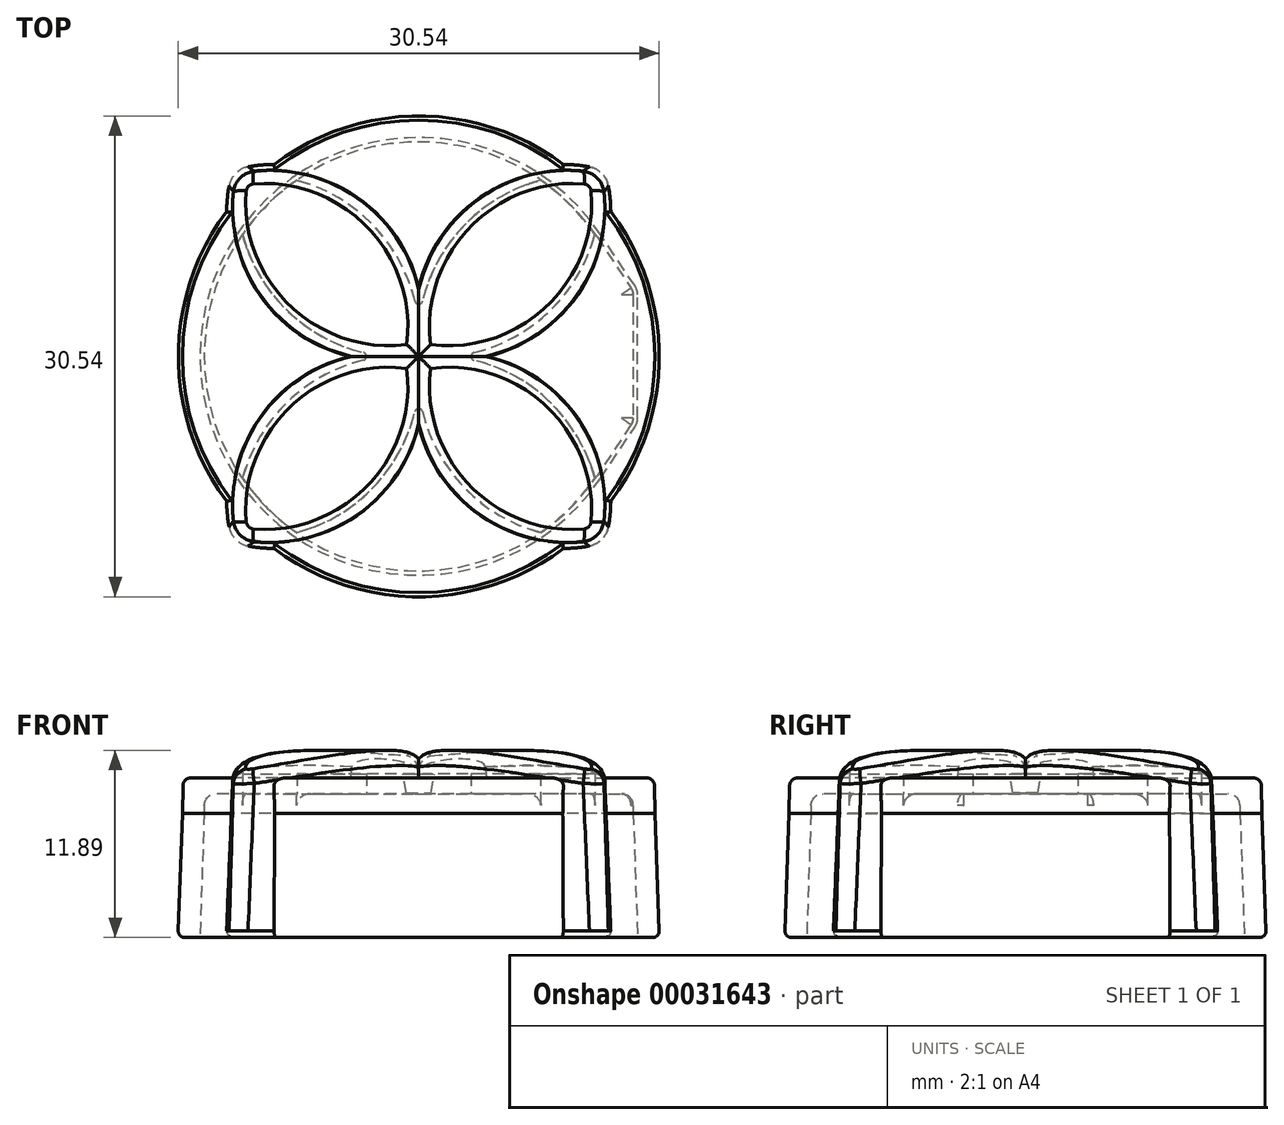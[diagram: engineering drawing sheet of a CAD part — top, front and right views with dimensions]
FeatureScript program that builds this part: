
annotation { "Feature Type Name" : "Feature", "Feature Type Description" : "" }
export const myFeature = defineFeature(function(context is Context, id is Id, definition is map)
    precondition{}
    {
        {
            var Q0;
            Q0=qCreatedBy(makeId("Top.planeOp"),FACE);
            cPlane(context, id + "F0", {"entities" : qUnion([Q0]), "cplaneType" : CPlaneType.OFFSET, "offset" : 8.73 * mm, "width" : 150 * mm, "height" : 150 * mm});
        }
        {
            var Q0;
            Q0=qCreatedBy(id+"F0.planeOp",FACE);
            var sketch = newSketch(context, id + "F1", { "sketchPlane" : qUnion([Q0])});
            skCircle(sketch, "E0", {"center": v(0, 0) * mm, "radius": 12.38 * mm});
            skCircle(sketch, "E1", {"center": v(0, 0) * mm, "radius": 13.38 * mm});
            skLineSegment(sketch, "E2.bottom", {"start": v(12.37, 4.08) * mm, "end": v(13.37, 4.08) * mm});
            skLineSegment(sketch, "E2.top", {"start": v(12.37, -4.07) * mm, "end": v(13.37, -4.07) * mm});
            skLineSegment(sketch, "E2.left", {"start": v(12.37, 3.91) * mm, "end": v(12.37, -3.91) * mm});
            skLineSegment(sketch, "E2.right", {"start": v(13.37, 3.92) * mm, "end": v(13.37, -3.92) * mm});
            skLineSegment(sketch, "E3", {"start": v(12.28, 4.2) * mm, "end": v(9.95, 7.35) * mm});
            skLineSegment(sketch, "E4", {"start": v(13.3, 4.2) * mm, "end": v(11.1, 7.46) * mm});
            skLineSegment(sketch, "E5", {"start": v(12.28, -4.2) * mm, "end": v(9.95, -7.35) * mm});
            skLineSegment(sketch, "E6", {"start": v(13.3, -4.2) * mm, "end": v(11.1, -7.46) * mm});
            skPoint(sketch, "E7.visualSharp", {"position": v(13.37, 4.08) * mm});
            skArc(sketch, "E7.filletArc", {"start": v(13.37, 3.92) * mm, "mid": v(13.35, 4.07) * mm, "end": v(13.3, 4.2) * mm});
            skPoint(sketch, "E8.visualSharp", {"position": v(13.37, -4.07) * mm});
            skArc(sketch, "E8.filletArc", {"start": v(13.3, -4.2) * mm, "mid": v(13.35, -4.07) * mm, "end": v(13.38, -3.92) * mm});
            skPoint(sketch, "E9.visualSharp", {"position": v(12.37, -4.07) * mm});
            skArc(sketch, "E9.filletArc", {"start": v(12.28, -4.2) * mm, "mid": v(12.35, -4.07) * mm, "end": v(12.38, -3.91) * mm});
            skPoint(sketch, "E10.visualSharp", {"position": v(12.37, 4.08) * mm});
            skArc(sketch, "E10.filletArc", {"start": v(12.38, 3.91) * mm, "mid": v(12.35, 4.07) * mm, "end": v(12.28, 4.2) * mm});
            skCircle(sketch, "E11.0", {"center": v(0, 0) * mm, "radius": 13.63 * mm});
            skLineSegment(sketch, "E12.0", {"start": v(13.5, 4.34) * mm, "end": v(11.31, 7.6) * mm});
            skArc(sketch, "E13.0", {"start": v(13.63, 3.92) * mm, "mid": v(13.6, 4.14) * mm, "end": v(13.5, 4.34) * mm});
            skLineSegment(sketch, "E14.0", {"start": v(13.63, 3.92) * mm, "end": v(13.63, -3.92) * mm});
            skArc(sketch, "E15.0", {"start": v(13.5, -4.34) * mm, "mid": v(13.6, -4.14) * mm, "end": v(13.63, -3.92) * mm});
            skLineSegment(sketch, "E16.0", {"start": v(13.5, -4.34) * mm, "end": v(11.31, -7.6) * mm});
            skCircle(sketch, "E17", {"center": v(0, 0) * mm, "radius": 15 * mm});
            skSolve(sketch);
        }
        {
            var Q0;
            {var subQ6=sQuery(id+"F1.wireOp",EDGE,"E12.0");Q0=makeQuery(id+"F1.imprint","IMPRINT",FACE,{"disambiguationData":[TD([[makeQuery(id+"F1.imprint","IMPRINT",EDGE,{"derivedFrom":subQ6}),-1.0]])]});}
            var Q1;
            {var subQ0=sQuery(id+"F1.wireOp",EDGE,"E0");var subQ3=makeQuery(id+"F1.imprint","INTERSECT",VERTEX,{"derivedFrom":[subQ0,sQuery(id+"F1.wireOp",EDGE,"E3")]});Q1=makeQuery(id+"F1.imprint","IMPRINT",FACE,{"disambiguationData":[TD([[makeQuery(id+"F1.imprint","IMPRINT",EDGE,{"disambiguationData":[TD([[subQ3,1.0]])],"derivedFrom":subQ0}),1.0]])]});}
            var Q2;
            {var subQ5=sQuery(id+"F1.wireOp",EDGE,"E4");var subQ7=sQuery(id+"F1.wireOp",EDGE,"E1");var subQ9=makeQuery(id+"F1.imprint","INTERSECT",VERTEX,{"derivedFrom":[subQ7,subQ5]});Q2=makeQuery(id+"F1.imprint","IMPRINT",FACE,{"disambiguationData":[TD([[makeQuery(id+"F1.imprint","IMPRINT",EDGE,{"disambiguationData":[TD([[subQ9,-1.0]])],"derivedFrom":subQ7}),-1.0]])]});}
            var Q3;
            {var subQ1=sQuery(id+"F1.wireOp",EDGE,"E3");Q3=makeQuery(id+"F1.imprint","IMPRINT",FACE,{"disambiguationData":[TD([[makeQuery(id+"F1.imprint","IMPRINT",EDGE,{"derivedFrom":subQ1}),-1.0]])]});}
            var Q4;
            {var subQ1=sQuery(id+"F1.wireOp",EDGE,"E3");Q4=makeQuery(id+"F1.imprint","IMPRINT",FACE,{"disambiguationData":[TD([[makeQuery(id+"F1.imprint","IMPRINT",EDGE,{"derivedFrom":subQ1}),1.0]])]});}
            var Q5;
            {var subQ3=sQuery(id+"F1.wireOp",EDGE,"E2.bottom");var subQ5=sQuery(id+"F1.wireOp",EDGE,"E7.filletArc");var subQ6=makeQuery(id+"F1.imprint","INTERSECT",VERTEX,{"derivedFrom":[subQ3,subQ5]});Q5=makeQuery(id+"F1.imprint","IMPRINT",FACE,{"disambiguationData":[TD([[makeQuery(id+"F1.imprint","IMPRINT",EDGE,{"disambiguationData":[TD([[subQ6,1.0]])],"derivedFrom":subQ3}),1.0]])]});}
            var Q6;
            {var subQ3=sQuery(id+"F1.wireOp",EDGE,"E2.bottom");var subQ5=sQuery(id+"F1.wireOp",EDGE,"E7.filletArc");var subQ6=makeQuery(id+"F1.imprint","INTERSECT",VERTEX,{"derivedFrom":[subQ3,subQ5]});Q6=makeQuery(id+"F1.imprint","IMPRINT",FACE,{"disambiguationData":[TD([[makeQuery(id+"F1.imprint","IMPRINT",EDGE,{"disambiguationData":[TD([[subQ6,1.0]])],"derivedFrom":subQ3}),-1.0]])]});}
            var Q7;
            {var subQ3=sQuery(id+"F1.wireOp",EDGE,"E2.bottom");var subQ5=sQuery(id+"F1.wireOp",EDGE,"E1");var subQ7=makeQuery(id+"F1.imprint","INTERSECT",VERTEX,{"derivedFrom":[subQ5,subQ3]});Q7=makeQuery(id+"F1.imprint","IMPRINT",FACE,{"disambiguationData":[TD([[makeQuery(id+"F1.imprint","IMPRINT",EDGE,{"disambiguationData":[TD([[subQ7,1.0]])],"derivedFrom":subQ5}),-1.0]])]});}
            var Q8;
            {var subQ1=sQuery(id+"F1.wireOp",EDGE,"E4");var subQ5=sQuery(id+"F1.wireOp",EDGE,"E1");var subQ6=makeQuery(id+"F1.imprint","INTERSECT",VERTEX,{"derivedFrom":[subQ5,subQ1]});Q8=makeQuery(id+"F1.imprint","IMPRINT",FACE,{"disambiguationData":[TD([[makeQuery(id+"F1.imprint","IMPRINT",EDGE,{"disambiguationData":[TD([[subQ6,1.0]])],"derivedFrom":subQ5}),-1.0]])]});}
            var Q9;
            {var subQ4=sQuery(id+"F1.wireOp",EDGE,"E12.0");Q9=makeQuery(id+"F1.imprint","IMPRINT",FACE,{"disambiguationData":[TD([[makeQuery(id+"F1.imprint","IMPRINT",EDGE,{"derivedFrom":subQ4}),1.0]])]});}
            var Q10;
            {var subQ2=sQuery(id+"F1.wireOp",EDGE,"E2.right");var subQ5=makeQuery(id+"F1.imprint","INTERSECT",VERTEX,{"derivedFrom":[sQuery(id+"F1.wireOp",EDGE,"E1"),subQ2]});Q10=makeQuery(id+"F1.imprint","IMPRINT",FACE,{"disambiguationData":[TD([[makeQuery(id+"F1.imprint","IMPRINT",EDGE,{"disambiguationData":[TD([[subQ5,1.0]])],"derivedFrom":subQ2}),1.0]])]});}
            var Q11;
            {var subQ1=sQuery(id+"F1.wireOp",EDGE,"E5");Q11=makeQuery(id+"F1.imprint","IMPRINT",FACE,{"disambiguationData":[TD([[makeQuery(id+"F1.imprint","IMPRINT",EDGE,{"derivedFrom":subQ1}),-1.0]])]});}
            var Q12;
            {var subQ3=sQuery(id+"F1.wireOp",EDGE,"E2.top");var subQ5=sQuery(id+"F1.wireOp",EDGE,"E8.filletArc");var subQ6=makeQuery(id+"F1.imprint","INTERSECT",VERTEX,{"derivedFrom":[subQ3,subQ5]});Q12=makeQuery(id+"F1.imprint","IMPRINT",FACE,{"disambiguationData":[TD([[makeQuery(id+"F1.imprint","IMPRINT",EDGE,{"disambiguationData":[TD([[subQ6,1.0]])],"derivedFrom":subQ3}),1.0]])]});}
            var Q13;
            {var subQ3=sQuery(id+"F1.wireOp",EDGE,"E2.top");var subQ5=sQuery(id+"F1.wireOp",EDGE,"E1");var subQ7=makeQuery(id+"F1.imprint","INTERSECT",VERTEX,{"derivedFrom":[subQ5,subQ3]});Q13=makeQuery(id+"F1.imprint","IMPRINT",FACE,{"disambiguationData":[TD([[makeQuery(id+"F1.imprint","IMPRINT",EDGE,{"disambiguationData":[TD([[subQ7,-1.0]])],"derivedFrom":subQ5}),-1.0]])]});}
            var Q14;
            {var subQ0=sQuery(id+"F1.wireOp",EDGE,"E15.0");Q14=makeQuery(id+"F1.imprint","IMPRINT",FACE,{"disambiguationData":[TD([[makeQuery(id+"F1.imprint","IMPRINT",EDGE,{"derivedFrom":subQ0}),1.0]])]});}
            var Q15;
            {var subQ1=sQuery(id+"F1.wireOp",EDGE,"E6");var subQ5=sQuery(id+"F1.wireOp",EDGE,"E1");var subQ6=makeQuery(id+"F1.imprint","INTERSECT",VERTEX,{"derivedFrom":[subQ5,subQ1]});Q15=makeQuery(id+"F1.imprint","IMPRINT",FACE,{"disambiguationData":[TD([[makeQuery(id+"F1.imprint","IMPRINT",EDGE,{"disambiguationData":[TD([[subQ6,-1.0]])],"derivedFrom":subQ5}),-1.0]])]});}
            var Q16;
            {var subQ3=sQuery(id+"F1.wireOp",EDGE,"E2.top");var subQ5=sQuery(id+"F1.wireOp",EDGE,"E8.filletArc");var subQ6=makeQuery(id+"F1.imprint","INTERSECT",VERTEX,{"derivedFrom":[subQ3,subQ5]});Q16=makeQuery(id+"F1.imprint","IMPRINT",FACE,{"disambiguationData":[TD([[makeQuery(id+"F1.imprint","IMPRINT",EDGE,{"disambiguationData":[TD([[subQ6,1.0]])],"derivedFrom":subQ3}),-1.0]])]});}
            extrude(context, id + "F2", {"entities" : qUnion([Q0, Q1, Q2, Q3, Q4, Q5, Q6, Q7, Q8, Q9, Q10, Q11, Q12, Q13, Q14, Q15, Q16]), "depth" : 2.25 * mm, "hasDraft" : true, "draftAngle" : 1 * degree, "draftPullDirection" : true});
        }
        {
            var Q0;
            {var subQ6=sQuery(id+"F1.wireOp",EDGE,"E12.0");Q0=makeQuery(id+"F1.imprint","IMPRINT",FACE,{"disambiguationData":[TD([[makeQuery(id+"F1.imprint","IMPRINT",EDGE,{"derivedFrom":subQ6}),-1.0]])]});}
            var Q1;
            {var subQ1=sQuery(id+"F1.wireOp",EDGE,"E3");Q1=makeQuery(id+"F1.imprint","IMPRINT",FACE,{"disambiguationData":[TD([[makeQuery(id+"F1.imprint","IMPRINT",EDGE,{"derivedFrom":subQ1}),-1.0]])]});}
            var Q2;
            {var subQ5=sQuery(id+"F1.wireOp",EDGE,"E4");var subQ7=sQuery(id+"F1.wireOp",EDGE,"E1");var subQ9=makeQuery(id+"F1.imprint","INTERSECT",VERTEX,{"derivedFrom":[subQ7,subQ5]});Q2=makeQuery(id+"F1.imprint","IMPRINT",FACE,{"disambiguationData":[TD([[makeQuery(id+"F1.imprint","IMPRINT",EDGE,{"disambiguationData":[TD([[subQ9,-1.0]])],"derivedFrom":subQ7}),-1.0]])]});}
            var Q3;
            {var subQ1=sQuery(id+"F1.wireOp",EDGE,"E3");Q3=makeQuery(id+"F1.imprint","IMPRINT",FACE,{"disambiguationData":[TD([[makeQuery(id+"F1.imprint","IMPRINT",EDGE,{"derivedFrom":subQ1}),1.0]])]});}
            var Q4;
            {var subQ0=sQuery(id+"F1.wireOp",EDGE,"E0");var subQ3=makeQuery(id+"F1.imprint","INTERSECT",VERTEX,{"derivedFrom":[subQ0,sQuery(id+"F1.wireOp",EDGE,"E3")]});Q4=makeQuery(id+"F1.imprint","IMPRINT",FACE,{"disambiguationData":[TD([[makeQuery(id+"F1.imprint","IMPRINT",EDGE,{"disambiguationData":[TD([[subQ3,1.0]])],"derivedFrom":subQ0}),1.0]])]});}
            var Q5;
            {var subQ1=sQuery(id+"F1.wireOp",EDGE,"E4");var subQ5=sQuery(id+"F1.wireOp",EDGE,"E1");var subQ6=makeQuery(id+"F1.imprint","INTERSECT",VERTEX,{"derivedFrom":[subQ5,subQ1]});Q5=makeQuery(id+"F1.imprint","IMPRINT",FACE,{"disambiguationData":[TD([[makeQuery(id+"F1.imprint","IMPRINT",EDGE,{"disambiguationData":[TD([[subQ6,1.0]])],"derivedFrom":subQ5}),-1.0]])]});}
            var Q6;
            {var subQ4=sQuery(id+"F1.wireOp",EDGE,"E12.0");Q6=makeQuery(id+"F1.imprint","IMPRINT",FACE,{"disambiguationData":[TD([[makeQuery(id+"F1.imprint","IMPRINT",EDGE,{"derivedFrom":subQ4}),1.0]])]});}
            var Q7;
            {var subQ3=sQuery(id+"F1.wireOp",EDGE,"E2.bottom");var subQ5=sQuery(id+"F1.wireOp",EDGE,"E7.filletArc");var subQ6=makeQuery(id+"F1.imprint","INTERSECT",VERTEX,{"derivedFrom":[subQ3,subQ5]});Q7=makeQuery(id+"F1.imprint","IMPRINT",FACE,{"disambiguationData":[TD([[makeQuery(id+"F1.imprint","IMPRINT",EDGE,{"disambiguationData":[TD([[subQ6,1.0]])],"derivedFrom":subQ3}),1.0]])]});}
            var Q8;
            {var subQ3=sQuery(id+"F1.wireOp",EDGE,"E2.bottom");var subQ5=sQuery(id+"F1.wireOp",EDGE,"E7.filletArc");var subQ6=makeQuery(id+"F1.imprint","INTERSECT",VERTEX,{"derivedFrom":[subQ3,subQ5]});Q8=makeQuery(id+"F1.imprint","IMPRINT",FACE,{"disambiguationData":[TD([[makeQuery(id+"F1.imprint","IMPRINT",EDGE,{"disambiguationData":[TD([[subQ6,1.0]])],"derivedFrom":subQ3}),-1.0]])]});}
            var Q9;
            {var subQ3=sQuery(id+"F1.wireOp",EDGE,"E2.bottom");var subQ5=sQuery(id+"F1.wireOp",EDGE,"E1");var subQ7=makeQuery(id+"F1.imprint","INTERSECT",VERTEX,{"derivedFrom":[subQ5,subQ3]});Q9=makeQuery(id+"F1.imprint","IMPRINT",FACE,{"disambiguationData":[TD([[makeQuery(id+"F1.imprint","IMPRINT",EDGE,{"disambiguationData":[TD([[subQ7,1.0]])],"derivedFrom":subQ5}),-1.0]])]});}
            var Q10;
            {var subQ2=sQuery(id+"F1.wireOp",EDGE,"E2.right");var subQ5=makeQuery(id+"F1.imprint","INTERSECT",VERTEX,{"derivedFrom":[sQuery(id+"F1.wireOp",EDGE,"E1"),subQ2]});Q10=makeQuery(id+"F1.imprint","IMPRINT",FACE,{"disambiguationData":[TD([[makeQuery(id+"F1.imprint","IMPRINT",EDGE,{"disambiguationData":[TD([[subQ5,1.0]])],"derivedFrom":subQ2}),1.0]])]});}
            var Q11;
            {var subQ1=sQuery(id+"F1.wireOp",EDGE,"E5");Q11=makeQuery(id+"F1.imprint","IMPRINT",FACE,{"disambiguationData":[TD([[makeQuery(id+"F1.imprint","IMPRINT",EDGE,{"derivedFrom":subQ1}),-1.0]])]});}
            var Q12;
            {var subQ3=sQuery(id+"F1.wireOp",EDGE,"E2.top");var subQ5=sQuery(id+"F1.wireOp",EDGE,"E8.filletArc");var subQ6=makeQuery(id+"F1.imprint","INTERSECT",VERTEX,{"derivedFrom":[subQ3,subQ5]});Q12=makeQuery(id+"F1.imprint","IMPRINT",FACE,{"disambiguationData":[TD([[makeQuery(id+"F1.imprint","IMPRINT",EDGE,{"disambiguationData":[TD([[subQ6,1.0]])],"derivedFrom":subQ3}),1.0]])]});}
            var Q13;
            {var subQ3=sQuery(id+"F1.wireOp",EDGE,"E2.top");var subQ5=sQuery(id+"F1.wireOp",EDGE,"E1");var subQ7=makeQuery(id+"F1.imprint","INTERSECT",VERTEX,{"derivedFrom":[subQ5,subQ3]});Q13=makeQuery(id+"F1.imprint","IMPRINT",FACE,{"disambiguationData":[TD([[makeQuery(id+"F1.imprint","IMPRINT",EDGE,{"disambiguationData":[TD([[subQ7,-1.0]])],"derivedFrom":subQ5}),-1.0]])]});}
            var Q14;
            {var subQ0=sQuery(id+"F1.wireOp",EDGE,"E15.0");Q14=makeQuery(id+"F1.imprint","IMPRINT",FACE,{"disambiguationData":[TD([[makeQuery(id+"F1.imprint","IMPRINT",EDGE,{"derivedFrom":subQ0}),1.0]])]});}
            var Q15;
            {var subQ3=sQuery(id+"F1.wireOp",EDGE,"E2.top");var subQ5=sQuery(id+"F1.wireOp",EDGE,"E8.filletArc");var subQ6=makeQuery(id+"F1.imprint","INTERSECT",VERTEX,{"derivedFrom":[subQ3,subQ5]});Q15=makeQuery(id+"F1.imprint","IMPRINT",FACE,{"disambiguationData":[TD([[makeQuery(id+"F1.imprint","IMPRINT",EDGE,{"disambiguationData":[TD([[subQ6,1.0]])],"derivedFrom":subQ3}),-1.0]])]});}
            var Q16;
            {var subQ1=sQuery(id+"F1.wireOp",EDGE,"E6");var subQ5=sQuery(id+"F1.wireOp",EDGE,"E1");var subQ6=makeQuery(id+"F1.imprint","INTERSECT",VERTEX,{"derivedFrom":[subQ5,subQ1]});Q16=makeQuery(id+"F1.imprint","IMPRINT",FACE,{"disambiguationData":[TD([[makeQuery(id+"F1.imprint","IMPRINT",EDGE,{"disambiguationData":[TD([[subQ6,-1.0]])],"derivedFrom":subQ5}),-1.0]])]});}
            extrude(context, id + "F3", {"entities" : qUnion([Q0, Q1, Q2, Q3, Q4, Q5, Q6, Q7, Q8, Q9, Q10, Q11, Q12, Q13, Q14, Q15, Q16]), "operationType" : NewBodyOperationType.ADD, "oppositeDirection" : true, "depth" : 7.88 * mm, "hasDraft" : true, "draftAngle" : 2 * degree});
        }
        {
            var Q0;
            Q0=qCreatedBy(makeId("Top.planeOp"),FACE);
            var sketch = newSketch(context, id + "F4", { "sketchPlane" : qUnion([Q0])});
            skLineSegment(sketch, "E18", {"start": v(0, 0) * mm, "end": v(0, 19.92) * mm, "construction": true});
            skLineSegment(sketch, "E19", {"start": v(0, 0) * mm, "end": v(17.2, 17.2) * mm, "construction": true});
            skArc(sketch, "E20", {"start": v(11.84, 11.84) * mm, "mid": v(2.38, 9.47) * mm, "end": v(0, 0) * mm});
            skArc(sketch, "E21.0.MirrorCS", {"start": v(11.84, 11.84) * mm, "mid": v(9.47, 2.38) * mm, "end": v(0, 0) * mm});
            skPoint(sketch, "E22.center", {"position": v(0, 0) * mm});
            skLineSegment(sketch, "E22.anchor1", {"start": v(0, 0) * mm, "end": v(0, 0) * mm});
            skLineSegment(sketch, "E22.anchor2", {"start": v(0, 0) * mm, "end": v(21.18, 0) * mm, "construction": true});
            skSolve(sketch);
        }
        {
            var Q0;
            Q0=qCreatedBy(makeId("Top.planeOp"),FACE);
            cPlane(context, id + "F5", {"entities" : qUnion([Q0]), "cplaneType" : CPlaneType.OFFSET, "offset" : 13.98 * mm, "width" : 150 * mm, "height" : 150 * mm});
        }
        {
            var Q0;
            Q0=qCreatedBy(id+"F5.planeOp",FACE);
            var sketch = newSketch(context, id + "F6", { "sketchPlane" : qUnion([Q0])});
            skLineSegment(sketch, "E23", {"start": v(0, 0) * mm, "end": v(0, 1.45) * mm, "construction": true});
            skLineSegment(sketch, "E24", {"start": v(0, 0) * mm, "end": v(22.98, 22.98) * mm, "construction": true});
            skArc(sketch, "E25", {"start": v(11.5, 11.5) * mm, "mid": v(2.63, 8.86) * mm, "end": v(0, 0) * mm});
            skArc(sketch, "E26", {"start": v(11.84, 11.84) * mm, "mid": v(2.71, 9.13) * mm, "end": v(0, 0) * mm, "construction": true});
            skArc(sketch, "E27.0.MirrorCS", {"start": v(11.5, 11.5) * mm, "mid": v(8.86, 2.63) * mm, "end": v(0, 0) * mm});
            skSolve(sketch);
        }
        {
            var Q1;
            Q1=makeQuery(id+"F4.imprint","IMPRINT",FACE,{"disambiguationData":[TD([[makeQuery(id+"F4.imprint","IMPRINT",EDGE,{"derivedFrom":sQuery(id+"F4.wireOp",EDGE,"E20")}),1.0]])]});
            var Q2;
            Q2=makeQuery(id+"F6.imprint","IMPRINT",FACE,{"disambiguationData":[TD([[makeQuery(id+"F6.imprint","IMPRINT",EDGE,{"derivedFrom":sQuery(id+"F6.wireOp",EDGE,"E25")}),1.0]])]});
            loft(context, id + "F7", {"sheetProfilesArray" : [{ "sheetProfileEntities" : qUnion([Q1]) }, { "sheetProfileEntities" : qUnion([Q2]) }]});
        }
        {
            var Q0;
            Q0=qCreatedBy(makeId("Front.planeOp"),FACE);
            var Q1;
            Q1=qCreatedBy(makeId("Right.planeOp"),FACE);
            cPlane(context, id + "F8", {"entities" : qUnion([Q0, Q1]), "cplaneType" : CPlaneType.MID_PLANE, "offset" : 150 * mm, "flipAlignment" : true, "width" : 150 * mm, "height" : 150 * mm});
        }
        {
            var Q0;
            Q0=qCreatedBy(id+"F8.planeOp",FACE);
            var sketch = newSketch(context, id + "F9", { "sketchPlane" : qUnion([Q0])});
            skLineSegment(sketch, "E28", {"start": v(0, 0) * mm, "end": v(0, 14) * mm});
            skLineSegment(sketch, "E29", {"start": v(0, 0.85) * mm, "end": v(16.75, 0.85) * mm});
            skLineSegment(sketch, "E30", {"start": v(0, 11.23) * mm, "end": v(23.83, 11.23) * mm, "construction": true});
            skLineSegment(sketch, "E31", {"start": v(16.75, 0.85) * mm, "end": v(16.37, 11.24) * mm});
            skLineSegment(sketch, "E32", {"start": v(16.75, 0.85) * mm, "end": v(16.75, 14) * mm});
            skLineSegment(sketch, "E33", {"start": v(0, 14) * mm, "end": v(16.75, 14) * mm});
            skLineSegment(sketch, "E34", {"start": v(16.75, 0.85) * mm, "end": v(16.75, -1.44) * mm});
            skLineSegment(sketch, "E35", {"start": v(16.75, -1.44) * mm, "end": v(0, -1.44) * mm});
            skLineSegment(sketch, "E36", {"start": v(0, -1.44) * mm, "end": v(0, 0.85) * mm});
            skArc(sketch, "E37", {"start": v(16.38, 11.24) * mm, "mid": v(8.24, 12.67) * mm, "end": v(0, 12.23) * mm});
            skLineSegment(sketch, "E38", {"start": v(0, 12.73) * mm, "end": v(27.33, 12.73) * mm, "construction": true});
            skSolve(sketch);
        }
        {
            var Q0;
            Q0=makeQuery(id+"F9.imprint","IMPRINT",FACE,{"disambiguationData":[TD([[makeQuery(id+"F9.imprint","IMPRINT",EDGE,{"derivedFrom":sQuery(id+"F9.wireOp",EDGE,"E31")}),-1.0]])]});
            var Q1;
            {var subQ2=sQuery(id+"F9.wireOp",EDGE,"E29");Q1=makeQuery(id+"F9.imprint","IMPRINT",FACE,{"disambiguationData":[TD([[makeQuery(id+"F9.imprint","IMPRINT",EDGE,{"derivedFrom":subQ2}),-1.0]])]});}
            extrude(context, id + "F10", {"entities" : qUnion([Q0, Q1]), "operationType" : NewBodyOperationType.REMOVE, "endBound" : BoundingType.SYMMETRIC, "oppositeDirection" : true, "depth" : 12 * mm});
        }
        {
            var Q0;
            {var subQ0=sQuery(id+"F4.wireOp",EDGE,"E20");var subQ1=sQuery(id+"F4.wireOp",EDGE,"E21.0.MirrorCS");var subQ2=sQuery(id+"F6.wireOp",EDGE,"E25");var subQ3=sQuery(id+"F6.wireOp",EDGE,"E27.0.MirrorCS");Q0=makeQuery(id+"F7.opLoft","SWEPT_EDGE",EDGE,{"disambiguationData":[OSD([subQ0,subQ1,subQ2,subQ3]),TDD([makeQuery(id+"F4.imprint","INTERSECT",VERTEX,{"disambiguationData":[OD(0.0)],"derivedFrom":[subQ0,subQ1]}),makeQuery(id+"F6.imprint","INTERSECT",VERTEX,{"disambiguationData":[OD(0.0)],"derivedFrom":[subQ2,subQ3]})])]});}
            fillet(context, id + "F11", {"entities" : qUnion([Q0]), "radius" : 1.5 * mm, "tangentPropagation" : true, "allowEdgeOverflow" : false});
        }
        {
            var Q0;
            {var subQ0=sQuery(id+"F4.wireOp",EDGE,"E20");var subQ1=sQuery(id+"F4.wireOp",EDGE,"E21.0.MirrorCS");var subQ2=sQuery(id+"F6.wireOp",EDGE,"E25");var subQ3=sQuery(id+"F6.wireOp",EDGE,"E27.0.MirrorCS");Q0=makeQuery(id+"F10.boolean.opBoolean","INTERSECT",EDGE,{"derivedFrom":[makeQuery(id+"F7.opLoft","SWEPT_FACE",FACE,{"disambiguationData":[OSD([subQ0,subQ1,subQ2,subQ3]),TDD([makeQuery(id+"F4.imprint","INTERSECT",VERTEX,{"disambiguationData":[OD(0.0)],"derivedFrom":[subQ0,subQ1]}),makeQuery(id+"F4.imprint","INTERSECT",VERTEX,{"disambiguationData":[OD(1.0)],"derivedFrom":[subQ0,subQ1]}),makeQuery(id+"F4.imprint","IMPRINT",EDGE,{"derivedFrom":subQ1}),makeQuery(id+"F6.imprint","INTERSECT",VERTEX,{"disambiguationData":[OD(0.0)],"derivedFrom":[subQ2,subQ3]}),makeQuery(id+"F6.imprint","INTERSECT",VERTEX,{"disambiguationData":[OD(1.0)],"derivedFrom":[subQ2,subQ3]}),makeQuery(id+"F6.imprint","IMPRINT",EDGE,{"derivedFrom":subQ3})])]}),makeQuery(id+"F10.opExtrude","SWEPT_FACE",FACE,{"disambiguationData":[OSD([sQuery(id+"F9.wireOp",EDGE,"E37")])]})]});}
            fillet(context, id + "F12", {"entities" : qUnion([Q0]), "radius" : 1 * mm, "tangentPropagation" : true, "allowEdgeOverflow" : false});
        }
        {
            var Q0;
            Q0=makeQuery(id+"F7.opLoft","SWEPT_BODY",BODY,{"disambiguationData":[OSD([makeQuery(id+"F4.imprint","IMPRINT",FACE,{"disambiguationData":[TD([[makeQuery(id+"F4.imprint","IMPRINT",EDGE,{"derivedFrom":sQuery(id+"F4.wireOp",EDGE,"E20")}),1.0]])]}),makeQuery(id+"F6.imprint","IMPRINT",FACE,{"disambiguationData":[TD([[makeQuery(id+"F6.imprint","IMPRINT",EDGE,{"derivedFrom":sQuery(id+"F6.wireOp",EDGE,"E25")}),1.0]])]})])]});
            var Q1;
            Q1=sQuery(id+"F9.wireOp",EDGE,"E28");
            circularPattern(context, id + "F13", {"operationType" : NewBodyOperationType.ADD, "entities" : qUnion([Q0]), "axis" : qUnion([Q1]), "angle" : 90 * degree, "instanceCount" : round(4)});
        }
        {
            var Q0;
            {var subQ0=sQuery(id+"F1.wireOp",EDGE,"E0");var subQ3=makeQuery(id+"F1.imprint","INTERSECT",VERTEX,{"derivedFrom":[subQ0,sQuery(id+"F1.wireOp",EDGE,"E3")]});Q0=makeQuery(id+"F1.imprint","IMPRINT",FACE,{"disambiguationData":[TD([[makeQuery(id+"F1.imprint","IMPRINT",EDGE,{"disambiguationData":[TD([[subQ3,1.0]])],"derivedFrom":subQ0}),1.0]])]});}
            var Q1;
            {var subQ1=sQuery(id+"F1.wireOp",EDGE,"E3");Q1=makeQuery(id+"F1.imprint","IMPRINT",FACE,{"disambiguationData":[TD([[makeQuery(id+"F1.imprint","IMPRINT",EDGE,{"derivedFrom":subQ1}),-1.0]])]});}
            var Q2;
            {var subQ5=sQuery(id+"F1.wireOp",EDGE,"E4");var subQ7=sQuery(id+"F1.wireOp",EDGE,"E1");var subQ9=makeQuery(id+"F1.imprint","INTERSECT",VERTEX,{"derivedFrom":[subQ7,subQ5]});Q2=makeQuery(id+"F1.imprint","IMPRINT",FACE,{"disambiguationData":[TD([[makeQuery(id+"F1.imprint","IMPRINT",EDGE,{"disambiguationData":[TD([[subQ9,-1.0]])],"derivedFrom":subQ7}),-1.0]])]});}
            var Q3;
            {var subQ4=sQuery(id+"F1.wireOp",EDGE,"E12.0");Q3=makeQuery(id+"F1.imprint","IMPRINT",FACE,{"disambiguationData":[TD([[makeQuery(id+"F1.imprint","IMPRINT",EDGE,{"derivedFrom":subQ4}),1.0]])]});}
            var Q4;
            {var subQ3=sQuery(id+"F1.wireOp",EDGE,"E2.bottom");var subQ5=sQuery(id+"F1.wireOp",EDGE,"E7.filletArc");var subQ6=makeQuery(id+"F1.imprint","INTERSECT",VERTEX,{"derivedFrom":[subQ3,subQ5]});Q4=makeQuery(id+"F1.imprint","IMPRINT",FACE,{"disambiguationData":[TD([[makeQuery(id+"F1.imprint","IMPRINT",EDGE,{"disambiguationData":[TD([[subQ6,1.0]])],"derivedFrom":subQ3}),1.0]])]});}
            var Q5;
            {var subQ3=sQuery(id+"F1.wireOp",EDGE,"E2.bottom");var subQ5=sQuery(id+"F1.wireOp",EDGE,"E7.filletArc");var subQ6=makeQuery(id+"F1.imprint","INTERSECT",VERTEX,{"derivedFrom":[subQ3,subQ5]});Q5=makeQuery(id+"F1.imprint","IMPRINT",FACE,{"disambiguationData":[TD([[makeQuery(id+"F1.imprint","IMPRINT",EDGE,{"disambiguationData":[TD([[subQ6,1.0]])],"derivedFrom":subQ3}),-1.0]])]});}
            var Q6;
            {var subQ1=sQuery(id+"F1.wireOp",EDGE,"E3");Q6=makeQuery(id+"F1.imprint","IMPRINT",FACE,{"disambiguationData":[TD([[makeQuery(id+"F1.imprint","IMPRINT",EDGE,{"derivedFrom":subQ1}),1.0]])]});}
            var Q7;
            {var subQ3=sQuery(id+"F1.wireOp",EDGE,"E2.bottom");var subQ5=sQuery(id+"F1.wireOp",EDGE,"E1");var subQ7=makeQuery(id+"F1.imprint","INTERSECT",VERTEX,{"derivedFrom":[subQ5,subQ3]});Q7=makeQuery(id+"F1.imprint","IMPRINT",FACE,{"disambiguationData":[TD([[makeQuery(id+"F1.imprint","IMPRINT",EDGE,{"disambiguationData":[TD([[subQ7,1.0]])],"derivedFrom":subQ5}),-1.0]])]});}
            var Q8;
            {var subQ1=sQuery(id+"F1.wireOp",EDGE,"E4");var subQ5=sQuery(id+"F1.wireOp",EDGE,"E1");var subQ6=makeQuery(id+"F1.imprint","INTERSECT",VERTEX,{"derivedFrom":[subQ5,subQ1]});Q8=makeQuery(id+"F1.imprint","IMPRINT",FACE,{"disambiguationData":[TD([[makeQuery(id+"F1.imprint","IMPRINT",EDGE,{"disambiguationData":[TD([[subQ6,1.0]])],"derivedFrom":subQ5}),-1.0]])]});}
            var Q9;
            {var subQ1=sQuery(id+"F1.wireOp",EDGE,"E5");Q9=makeQuery(id+"F1.imprint","IMPRINT",FACE,{"disambiguationData":[TD([[makeQuery(id+"F1.imprint","IMPRINT",EDGE,{"derivedFrom":subQ1}),-1.0]])]});}
            var Q10;
            {var subQ3=sQuery(id+"F1.wireOp",EDGE,"E2.top");var subQ5=sQuery(id+"F1.wireOp",EDGE,"E1");var subQ7=makeQuery(id+"F1.imprint","INTERSECT",VERTEX,{"derivedFrom":[subQ5,subQ3]});Q10=makeQuery(id+"F1.imprint","IMPRINT",FACE,{"disambiguationData":[TD([[makeQuery(id+"F1.imprint","IMPRINT",EDGE,{"disambiguationData":[TD([[subQ7,-1.0]])],"derivedFrom":subQ5}),-1.0]])]});}
            var Q11;
            {var subQ1=sQuery(id+"F1.wireOp",EDGE,"E6");var subQ5=sQuery(id+"F1.wireOp",EDGE,"E1");var subQ6=makeQuery(id+"F1.imprint","INTERSECT",VERTEX,{"derivedFrom":[subQ5,subQ1]});Q11=makeQuery(id+"F1.imprint","IMPRINT",FACE,{"disambiguationData":[TD([[makeQuery(id+"F1.imprint","IMPRINT",EDGE,{"disambiguationData":[TD([[subQ6,-1.0]])],"derivedFrom":subQ5}),-1.0]])]});}
            var Q12;
            {var subQ3=sQuery(id+"F1.wireOp",EDGE,"E2.top");var subQ5=sQuery(id+"F1.wireOp",EDGE,"E8.filletArc");var subQ6=makeQuery(id+"F1.imprint","INTERSECT",VERTEX,{"derivedFrom":[subQ3,subQ5]});Q12=makeQuery(id+"F1.imprint","IMPRINT",FACE,{"disambiguationData":[TD([[makeQuery(id+"F1.imprint","IMPRINT",EDGE,{"disambiguationData":[TD([[subQ6,1.0]])],"derivedFrom":subQ3}),-1.0]])]});}
            var Q13;
            {var subQ0=sQuery(id+"F1.wireOp",EDGE,"E15.0");Q13=makeQuery(id+"F1.imprint","IMPRINT",FACE,{"disambiguationData":[TD([[makeQuery(id+"F1.imprint","IMPRINT",EDGE,{"derivedFrom":subQ0}),1.0]])]});}
            var Q14;
            {var subQ3=sQuery(id+"F1.wireOp",EDGE,"E2.top");var subQ5=sQuery(id+"F1.wireOp",EDGE,"E8.filletArc");var subQ6=makeQuery(id+"F1.imprint","INTERSECT",VERTEX,{"derivedFrom":[subQ3,subQ5]});Q14=makeQuery(id+"F1.imprint","IMPRINT",FACE,{"disambiguationData":[TD([[makeQuery(id+"F1.imprint","IMPRINT",EDGE,{"disambiguationData":[TD([[subQ6,1.0]])],"derivedFrom":subQ3}),1.0]])]});}
            var Q15;
            {var subQ2=sQuery(id+"F1.wireOp",EDGE,"E2.right");var subQ5=makeQuery(id+"F1.imprint","INTERSECT",VERTEX,{"derivedFrom":[sQuery(id+"F1.wireOp",EDGE,"E1"),subQ2]});Q15=makeQuery(id+"F1.imprint","IMPRINT",FACE,{"disambiguationData":[TD([[makeQuery(id+"F1.imprint","IMPRINT",EDGE,{"disambiguationData":[TD([[subQ5,1.0]])],"derivedFrom":subQ2}),1.0]])]});}
            extrude(context, id + "F14", {"entities" : qUnion([Q0, Q1, Q2, Q3, Q4, Q5, Q6, Q7, Q8, Q9, Q10, Q11, Q12, Q13, Q14, Q15]), "operationType" : NewBodyOperationType.REMOVE, "depth" : 1.25 * mm, "hasDraft" : true, "draftAngle" : 1 * degree, "draftPullDirection" : true, "hasSecondDirection" : true, "secondDirectionBound" : SecondDirectionBoundingType.THROUGH_ALL, "secondDirectionOppositeDirection" : true, "secondDirectionDepth" : 25 * mm, "hasSecondDirectionDraft" : true, "secondDirectionDraftAngle" : 2 * degree});
        }
        {
            var Q0;
            Q0=makeQuery(id+"F14.boolean.opBoolean","COPY",FACE,{"disambiguationData":[OD(0.0)],"derivedFrom":makeQuery(id+"F14.opExtrude","CAP_FACE",FACE,{"disambiguationData":[OSD([sQuery(id+"F1.wireOp",EDGE,"E11.0"),sQuery(id+"F1.wireOp",EDGE,"E12.0"),sQuery(id+"F1.wireOp",EDGE,"E13.0"),sQuery(id+"F1.wireOp",EDGE,"E14.0"),sQuery(id+"F1.wireOp",EDGE,"E15.0"),sQuery(id+"F1.wireOp",EDGE,"E16.0")])],"isStart":false})});
            var sketch = newSketch(context, id + "F15", { "sketchPlane" : qUnion([Q0])});
            skLineSegment(sketch, "E39", {"start": v(0, 0) * mm, "end": v(14.5, 14.5) * mm, "construction": true});
            skPoint(sketch, "E40.center", {"position": v(0, 0) * mm});
            skLineSegment(sketch, "E41", {"start": v(-34.97, -4.74) * mm, "end": v(-34.97, -3.29) * mm, "construction": true});
            skLineSegment(sketch, "E42", {"start": v(-34.97, -4.74) * mm, "end": v(-11.99, 18.24) * mm, "construction": true});
            skArc(sketch, "E43", {"start": v(-23.48, 6.75) * mm, "mid": v(-32.33, 4.11) * mm, "end": v(-34.97, -4.74) * mm});
            skArc(sketch, "E44", {"start": v(-23.12, 7.1) * mm, "mid": v(-32.25, 4.39) * mm, "end": v(-34.97, -4.74) * mm, "construction": true});
            skArc(sketch, "E45.0.MirrorCS", {"start": v(-23.48, 6.75) * mm, "mid": v(-26.11, -2.1) * mm, "end": v(-34.97, -4.74) * mm});
            skArc(sketch, "E46", {"start": v(11.5, 11.5) * mm, "mid": v(4.37, 9.6) * mm, "end": v(0.24, 3.51) * mm});
            skCircle(sketch, "E47", {"center": v(0, 0) * mm, "radius": 14 * mm});
            skArc(sketch, "E48.MirrorCS", {"start": v(11.5, 11.5) * mm, "mid": v(9.6, 4.37) * mm, "end": v(3.51, 0.24) * mm});
            skArc(sketch, "E49.1.0", {"start": v(-11.5, 11.5) * mm, "mid": v(-9.6, 4.37) * mm, "end": v(-3.51, 0.24) * mm});
            skArc(sketch, "E49.1.1", {"start": v(-11.5, 11.5) * mm, "mid": v(-4.37, 9.6) * mm, "end": v(-0.24, 3.51) * mm});
            skArc(sketch, "E49.2.0", {"start": v(-11.5, -11.5) * mm, "mid": v(-4.37, -9.6) * mm, "end": v(-0.24, -3.51) * mm});
            skArc(sketch, "E49.2.1", {"start": v(-11.5, -11.5) * mm, "mid": v(-9.6, -4.37) * mm, "end": v(-3.51, -0.24) * mm});
            skArc(sketch, "E49.3.0", {"start": v(11.5, -11.5) * mm, "mid": v(9.6, -4.37) * mm, "end": v(3.51, -0.24) * mm});
            skArc(sketch, "E49.3.1", {"start": v(11.5, -11.5) * mm, "mid": v(4.37, -9.6) * mm, "end": v(0.24, -3.51) * mm});
            skArc(sketch, "E50.filletArc", {"start": v(-0.24, 3.51) * mm, "mid": v(0, 3.32) * mm, "end": v(0.24, 3.51) * mm});
            skArc(sketch, "E51.filletArc", {"start": v(3.51, 0.24) * mm, "mid": v(3.32, 0) * mm, "end": v(3.51, -0.24) * mm});
            skArc(sketch, "E52.filletArc", {"start": v(0.24, -3.51) * mm, "mid": v(0, -3.32) * mm, "end": v(-0.24, -3.51) * mm});
            skArc(sketch, "E53.filletArc", {"start": v(-3.51, -0.24) * mm, "mid": v(-3.32, 0) * mm, "end": v(-3.51, 0.24) * mm});
            skSolve(sketch);
        }
        {
            var Q0;
            {var subQ11=sQuery(id+"F15.wireOp",EDGE,"E50.filletArc");Q0=makeQuery(id+"F15.imprint","IMPRINT",FACE,{"disambiguationData":[TD([[makeQuery(id+"F15.imprint","IMPRINT",EDGE,{"derivedFrom":subQ11}),-1.0]])]});}
            extrude(context, id + "F16", {"entities" : qUnion([Q0]), "operationType" : NewBodyOperationType.REMOVE, "oppositeDirection" : true, "depth" : 1.25 * mm});
        }
        {
            var Q0;
            Q0=makeQuery(id+"F14.boolean.opBoolean","COPY",EDGE,{"derivedFrom":makeQuery(id+"F14.opExtrude","CAP_EDGE",EDGE,{"disambiguationData":[OSD([sQuery(id+"F1.wireOp",EDGE,"E14.0")])],"isStart":false})});
            var Q1;
            {var subQ0=sQuery(id+"F1.wireOp",EDGE,"E11.0");var subQ1=makeQuery(id+"F14.boolean.opBoolean","COPY",EDGE,{"disambiguationData":[OD(0.0)],"derivedFrom":makeQuery(id+"F14.opExtrude","CAP_EDGE",EDGE,{"disambiguationData":[OSD([subQ0])],"isStart":false})});var subQ3=sQuery(id+"F15.wireOp",EDGE,"E46");Q1=makeQuery(id+"F16.boolean.opBoolean","SPLIT",EDGE,{"disambiguationData":[TD([makeQuery(id+"F16.opExtrude","SWEPT_FACE",FACE,{"disambiguationData":[OSD([subQ3])]})])],"derivedFrom":subQ1});}
            var Q2;
            {var subQ0=sQuery(id+"F1.wireOp",EDGE,"E11.0");var subQ1=makeQuery(id+"F14.boolean.opBoolean","COPY",EDGE,{"disambiguationData":[OD(0.0)],"derivedFrom":makeQuery(id+"F14.opExtrude","CAP_EDGE",EDGE,{"disambiguationData":[OSD([subQ0])],"isStart":false})});var subQ3=sQuery(id+"F15.wireOp",EDGE,"E49.2.0");Q2=makeQuery(id+"F16.boolean.opBoolean","SPLIT",EDGE,{"disambiguationData":[TD([makeQuery(id+"F16.opExtrude","SWEPT_FACE",FACE,{"disambiguationData":[OSD([subQ3])]})])],"derivedFrom":subQ1});}
            var Q3;
            {var subQ0=sQuery(id+"F1.wireOp",EDGE,"E11.0");var subQ1=makeQuery(id+"F14.boolean.opBoolean","COPY",EDGE,{"disambiguationData":[OD(0.0)],"derivedFrom":makeQuery(id+"F14.opExtrude","CAP_EDGE",EDGE,{"disambiguationData":[OSD([subQ0])],"isStart":false})});var subQ3=sQuery(id+"F15.wireOp",EDGE,"E49.1.0");Q3=makeQuery(id+"F16.boolean.opBoolean","SPLIT",EDGE,{"disambiguationData":[TD([makeQuery(id+"F16.opExtrude","SWEPT_FACE",FACE,{"disambiguationData":[OSD([subQ3])]})])],"derivedFrom":subQ1});}
            fillet(context, id + "F17", {"entities" : qUnion([Q0, Q1, Q2, Q3]), "radius" : .75 * mm, "tangentPropagation" : true, "allowEdgeOverflow" : false});
        }
        {
            var Q0;
            Q0=makeQuery(id+"F16.boolean.opBoolean","COPY",FACE,{"derivedFrom":makeQuery(id+"F16.opExtrude","CAP_FACE",FACE,{"disambiguationData":[OSD([sQuery(id+"F15.wireOp",EDGE,"E46"),sQuery(id+"F15.wireOp",EDGE,"E47"),sQuery(id+"F15.wireOp",EDGE,"E48.MirrorCS"),sQuery(id+"F15.wireOp",EDGE,"E49.1.0"),sQuery(id+"F15.wireOp",EDGE,"E49.1.1"),sQuery(id+"F15.wireOp",EDGE,"E49.2.0"),sQuery(id+"F15.wireOp",EDGE,"E49.2.1"),sQuery(id+"F15.wireOp",EDGE,"E49.3.0"),sQuery(id+"F15.wireOp",EDGE,"E49.3.1"),sQuery(id+"F15.wireOp",EDGE,"E50.filletArc"),sQuery(id+"F15.wireOp",EDGE,"E51.filletArc"),sQuery(id+"F15.wireOp",EDGE,"E52.filletArc"),sQuery(id+"F15.wireOp",EDGE,"E53.filletArc")])],"isStart":false})});
            var sketch = newSketch(context, id + "F18", { "sketchPlane" : qUnion([Q0])});
            skCircle(sketch, "E54", {"center": v(0, 0) * mm, "radius": 1 * mm});
            skSolve(sketch);
        }
        {
            var Q0;
            Q0=qSketchRegion(id+"F18",true);
            extrude(context, id + "F19", {"entities" : qUnion([Q0]), "operationType" : NewBodyOperationType.ADD, "depth" : 1.2 * mm, "hasDraft" : true, "draftAngle" : 10 * degree, "draftPullDirection" : true});
        }
        {
            var Q0;
            {var subQ0=sQuery(id+"F4.wireOp",EDGE,"E20");var subQ1=sQuery(id+"F4.wireOp",EDGE,"E21.0.MirrorCS");var subQ2=sQuery(id+"F6.wireOp",EDGE,"E25");var subQ3=sQuery(id+"F6.wireOp",EDGE,"E27.0.MirrorCS");Q0=makeQuery(id+"F13.opPattern","COPY",EDGE,{"derivedFrom":makeQuery(id+"F10.boolean.opBoolean","INTERSECT",EDGE,{"derivedFrom":[makeQuery(id+"F7.opLoft","SWEPT_FACE",FACE,{"disambiguationData":[OSD([subQ0,subQ1,subQ2,subQ3]),TDD([makeQuery(id+"F4.imprint","INTERSECT",VERTEX,{"disambiguationData":[OD(0.0)],"derivedFrom":[subQ0,subQ1]}),makeQuery(id+"F4.imprint","INTERSECT",VERTEX,{"disambiguationData":[OD(1.0)],"derivedFrom":[subQ0,subQ1]}),makeQuery(id+"F4.imprint","IMPRINT",EDGE,{"derivedFrom":subQ1}),makeQuery(id+"F6.imprint","INTERSECT",VERTEX,{"disambiguationData":[OD(0.0)],"derivedFrom":[subQ2,subQ3]}),makeQuery(id+"F6.imprint","INTERSECT",VERTEX,{"disambiguationData":[OD(1.0)],"derivedFrom":[subQ2,subQ3]}),makeQuery(id+"F6.imprint","IMPRINT",EDGE,{"derivedFrom":subQ3})])]}),makeQuery(id+"F10.opExtrude","SWEPT_FACE",FACE,{"disambiguationData":[OSD([sQuery(id+"F9.wireOp",EDGE,"E29")])]})]}),"instanceName":"3"});}
            var Q1;
            {var subQ0=sQuery(id+"F4.wireOp",EDGE,"E20");var subQ1=sQuery(id+"F4.wireOp",EDGE,"E21.0.MirrorCS");var subQ2=sQuery(id+"F6.wireOp",EDGE,"E25");var subQ3=sQuery(id+"F6.wireOp",EDGE,"E27.0.MirrorCS");Q1=makeQuery(id+"F10.boolean.opBoolean","INTERSECT",EDGE,{"derivedFrom":[makeQuery(id+"F7.opLoft","SWEPT_FACE",FACE,{"disambiguationData":[OSD([subQ0,subQ1,subQ2,subQ3]),TDD([makeQuery(id+"F4.imprint","INTERSECT",VERTEX,{"disambiguationData":[OD(0.0)],"derivedFrom":[subQ0,subQ1]}),makeQuery(id+"F4.imprint","INTERSECT",VERTEX,{"disambiguationData":[OD(1.0)],"derivedFrom":[subQ0,subQ1]}),makeQuery(id+"F4.imprint","IMPRINT",EDGE,{"derivedFrom":subQ1}),makeQuery(id+"F6.imprint","INTERSECT",VERTEX,{"disambiguationData":[OD(0.0)],"derivedFrom":[subQ2,subQ3]}),makeQuery(id+"F6.imprint","INTERSECT",VERTEX,{"disambiguationData":[OD(1.0)],"derivedFrom":[subQ2,subQ3]}),makeQuery(id+"F6.imprint","IMPRINT",EDGE,{"derivedFrom":subQ3})])]}),makeQuery(id+"F10.opExtrude","SWEPT_FACE",FACE,{"disambiguationData":[OSD([sQuery(id+"F9.wireOp",EDGE,"E29")])]})]});}
            var Q2;
            {var subQ0=sQuery(id+"F4.wireOp",EDGE,"E20");var subQ1=sQuery(id+"F4.wireOp",EDGE,"E21.0.MirrorCS");var subQ2=sQuery(id+"F6.wireOp",EDGE,"E25");var subQ3=sQuery(id+"F6.wireOp",EDGE,"E27.0.MirrorCS");Q2=makeQuery(id+"F13.opPattern","COPY",EDGE,{"derivedFrom":makeQuery(id+"F10.boolean.opBoolean","INTERSECT",EDGE,{"derivedFrom":[makeQuery(id+"F7.opLoft","SWEPT_FACE",FACE,{"disambiguationData":[OSD([subQ0,subQ1,subQ2,subQ3]),TDD([makeQuery(id+"F4.imprint","INTERSECT",VERTEX,{"disambiguationData":[OD(0.0)],"derivedFrom":[subQ0,subQ1]}),makeQuery(id+"F4.imprint","INTERSECT",VERTEX,{"disambiguationData":[OD(1.0)],"derivedFrom":[subQ0,subQ1]}),makeQuery(id+"F4.imprint","IMPRINT",EDGE,{"derivedFrom":subQ1}),makeQuery(id+"F6.imprint","INTERSECT",VERTEX,{"disambiguationData":[OD(0.0)],"derivedFrom":[subQ2,subQ3]}),makeQuery(id+"F6.imprint","INTERSECT",VERTEX,{"disambiguationData":[OD(1.0)],"derivedFrom":[subQ2,subQ3]}),makeQuery(id+"F6.imprint","IMPRINT",EDGE,{"derivedFrom":subQ3})])]}),makeQuery(id+"F10.opExtrude","SWEPT_FACE",FACE,{"disambiguationData":[OSD([sQuery(id+"F9.wireOp",EDGE,"E29")])]})]}),"instanceName":"1"});}
            var Q3;
            {var subQ0=sQuery(id+"F4.wireOp",EDGE,"E20");var subQ1=sQuery(id+"F4.wireOp",EDGE,"E21.0.MirrorCS");var subQ2=sQuery(id+"F6.wireOp",EDGE,"E25");var subQ3=sQuery(id+"F6.wireOp",EDGE,"E27.0.MirrorCS");Q3=makeQuery(id+"F13.opPattern","COPY",EDGE,{"derivedFrom":makeQuery(id+"F10.boolean.opBoolean","INTERSECT",EDGE,{"derivedFrom":[makeQuery(id+"F7.opLoft","SWEPT_FACE",FACE,{"disambiguationData":[OSD([subQ0,subQ1,subQ2,subQ3]),TDD([makeQuery(id+"F4.imprint","INTERSECT",VERTEX,{"disambiguationData":[OD(0.0)],"derivedFrom":[subQ0,subQ1]}),makeQuery(id+"F4.imprint","INTERSECT",VERTEX,{"disambiguationData":[OD(1.0)],"derivedFrom":[subQ0,subQ1]}),makeQuery(id+"F4.imprint","IMPRINT",EDGE,{"derivedFrom":subQ1}),makeQuery(id+"F6.imprint","INTERSECT",VERTEX,{"disambiguationData":[OD(0.0)],"derivedFrom":[subQ2,subQ3]}),makeQuery(id+"F6.imprint","INTERSECT",VERTEX,{"disambiguationData":[OD(1.0)],"derivedFrom":[subQ2,subQ3]}),makeQuery(id+"F6.imprint","IMPRINT",EDGE,{"derivedFrom":subQ3})])]}),makeQuery(id+"F10.opExtrude","SWEPT_FACE",FACE,{"disambiguationData":[OSD([sQuery(id+"F9.wireOp",EDGE,"E29")])]})]}),"instanceName":"2"});}
            var Q4;
            Q4=makeQuery(id+"F3.opExtrude","CAP_EDGE",EDGE,{"disambiguationData":[OSD([sQuery(id+"F1.wireOp",EDGE,"E17")])],"isStart":false});
            fillet(context, id + "F20", {"entities" : qUnion([Q0, Q1, Q2, Q3, Q4]), "radius" : .4 * mm, "tangentPropagation" : true, "allowEdgeOverflow" : false});
        }
        {
            var Q0;
            Q0=makeQuery(id+"F2.opExtrude","CAP_EDGE",EDGE,{"disambiguationData":[OSD([sQuery(id+"F1.wireOp",EDGE,"E17")])],"isStart":false});
            fillet(context, id + "F21", {"entities" : qUnion([Q0]), "radius" : .5 * mm, "tangentPropagation" : true, "allowEdgeOverflow" : false});
        }
    });
